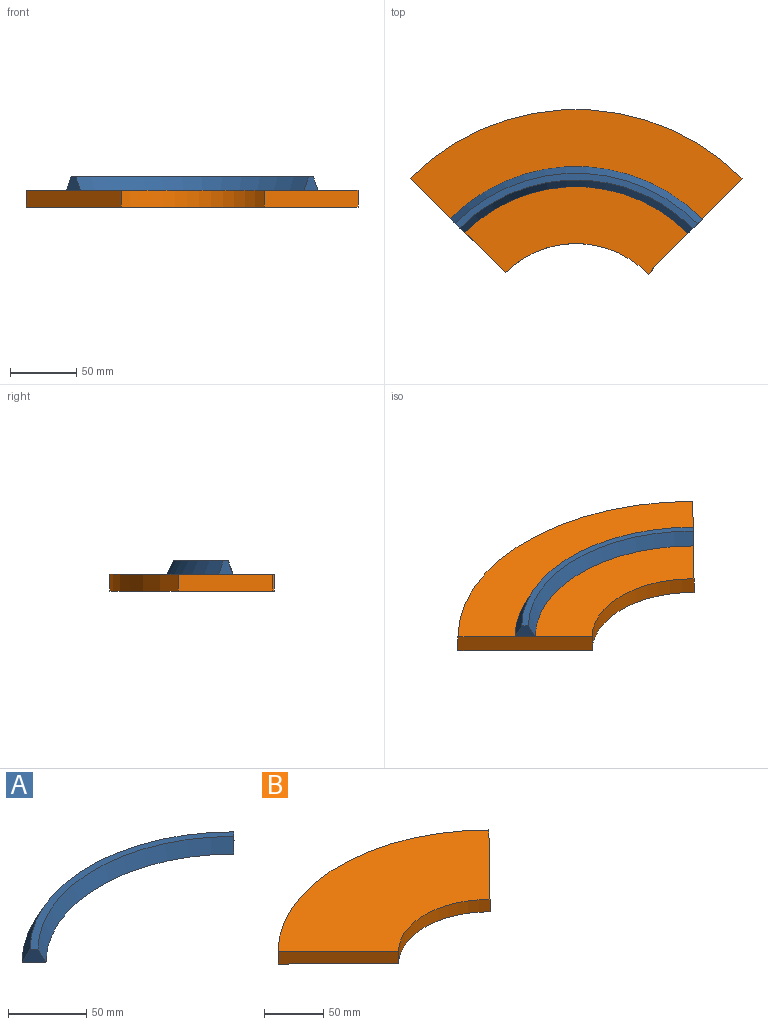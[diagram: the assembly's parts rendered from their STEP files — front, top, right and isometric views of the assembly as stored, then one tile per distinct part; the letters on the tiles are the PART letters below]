
ASSEMBLY  parts=2 mates=1
PART A: 6 faces, bbox 190.8x50.6x10.2 mm
  f0: plane 10.82x10.73mm, normal (0.7,-0.71,0), area 103.2mm2, adj f2,f3,f4,f5
  f1: plane 10.78x10.78mm, normal (-0.71,-0.71,0), area 103.2mm2, adj f2,f3,f4,f5
  f2: plane 183.57x41.9mm, normal (0,0,1), area 1016.1mm2, adj f0,f1,f3,f5
  f3: cone r=129.54mm half-angle=26.6deg, axis (0,0,-1), area 2362.9mm2, adj f0,f1,f2,f4
  f4: plane 190.77x50.55mm, normal (0,0,-1), area 3048.2mm2, adj f0,f1,f3,f5
  f5: cone r=119.38mm half-angle=26.6deg, axis (0,0,1), area 2181.1mm2, adj f0,f1,f2,f4
PART B: 6 faces, bbox 251.5x124.6x12.7 mm
  f0: plane 72.51x71.17mm, normal (0.71,-0.7,0), area 1290.3mm2, adj f1,f3,f4,f5
  f1: cylinder r=177.79mm len=251.5mm, axis (0,0,1), area 3547.9mm2, adj f0,f2,f4,f5
  f2: plane 72.09x71.58mm, normal (-0.7,-0.71,0), area 1290.2mm2, adj f1,f3,f4,f5
  f3: cylinder r=76.2mm len=108.24mm, axis (0,0,1), area 1528.8mm2, adj f0,f2,f4,f5
  f4: plane 251.5x124.62mm, normal (0,0,-1), area 20304.7mm2, adj f0,f1,f2,f3
  f5: plane 251.5x124.62mm, normal (0,0,1), area 20304.7mm2, adj f0,f1,f2,f3
PLACE A t=(39.99,-297.04,-118.83)mm
PLACE B t=(40,-297.03,-118.83)mm
MATE fastened A.f4 <-> B.f5  axis (0,0,-1) through (130.16,-207.6,-118.83)mm
